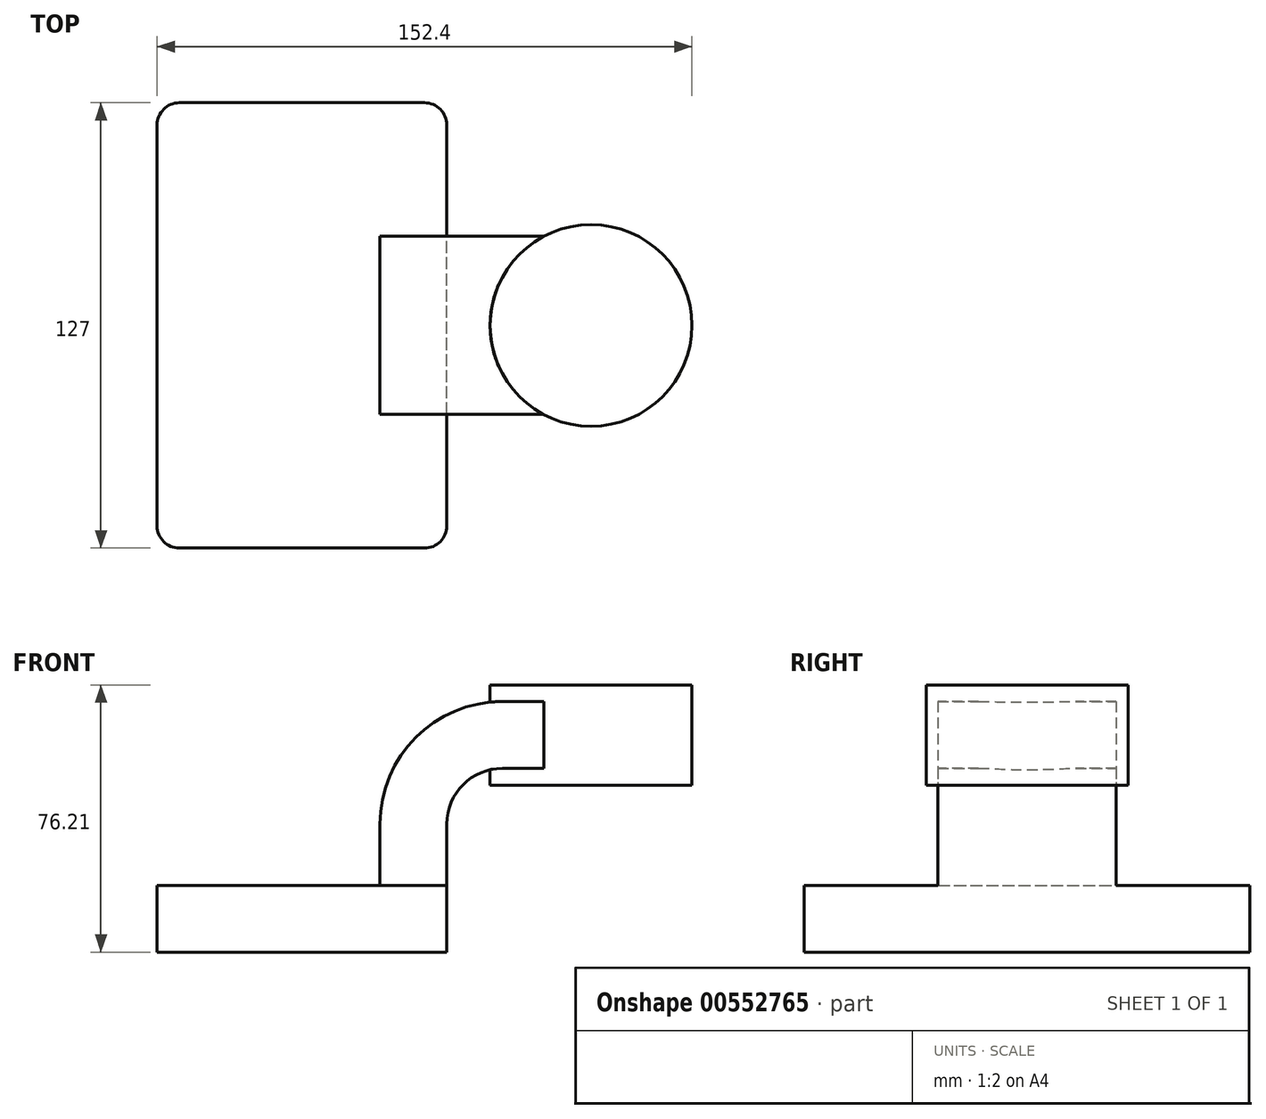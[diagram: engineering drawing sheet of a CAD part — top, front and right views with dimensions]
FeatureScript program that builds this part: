
annotation { "Feature Type Name" : "Feature", "Feature Type Description" : "" }
export const myFeature = defineFeature(function(context is Context, id is Id, definition is map)
    precondition{}
    {
        {
            var Q0;
            Q0=qCreatedBy(makeId("Front.planeOp"),FACE);
            var sketch = newSketch(context, id + "F0", { "sketchPlane" : qUnion([Q0])});
            skLineSegment(sketch, "E0.bottom", {"start": v(-41.28, 9.52) * mm, "end": v(41.28, 9.52) * mm});
            skLineSegment(sketch, "E0.top", {"start": v(-41.28, -9.53) * mm, "end": v(41.28, -9.53) * mm});
            skLineSegment(sketch, "E0.left", {"start": v(-41.28, 9.52) * mm, "end": v(-41.28, -9.53) * mm});
            skLineSegment(sketch, "E0.right", {"start": v(41.28, 9.52) * mm, "end": v(41.28, -9.53) * mm});
            skPoint(sketch, "E0.middle", {"position": v(0, 0) * mm});
            skLineSegment(sketch, "E1.bottom", {"start": v(111.13, 38.1) * mm, "end": v(60.33, 38.1) * mm});
            skLineSegment(sketch, "E1.top", {"start": v(111.13, 66.68) * mm, "end": v(60.33, 66.68) * mm});
            skLineSegment(sketch, "E1.left", {"start": v(111.13, 38.1) * mm, "end": v(111.13, 66.68) * mm});
            skLineSegment(sketch, "E1.right", {"start": v(60.33, 38.1) * mm, "end": v(60.33, 66.67) * mm});
            skPoint(sketch, "E1.middle", {"position": v(85.73, 52.39) * mm});
            skLineSegment(sketch, "E2", {"start": v(41.28, 9.52) * mm, "end": v(41.28, 27) * mm});
            skArc(sketch, "E3", {"start": v(41.28, 27) * mm, "mid": v(45.92, 38.23) * mm, "end": v(57.15, 42.88) * mm});
            skLineSegment(sketch, "E4", {"start": v(57.15, 42.88) * mm, "end": v(82.37, 42.88) * mm});
            skLineSegment(sketch, "E5.0", {"start": v(57.15, 61.93) * mm, "end": v(82.37, 61.93) * mm});
            skArc(sketch, "E5.1", {"start": v(22.23, 27) * mm, "mid": v(32.45, 51.7) * mm, "end": v(57.15, 61.93) * mm});
            skLineSegment(sketch, "E5.2", {"start": v(22.23, 9.53) * mm, "end": v(22.22, 27) * mm});
            skLineSegment(sketch, "E6", {"start": v(82.37, 38.1) * mm, "end": v(82.37, 66.68) * mm});
            skPoint(sketch, "E6.startSnap0", {"position": v(85.73, 38.1) * mm});
            skFitSpline(sketch, "E7", {"points": [v(-41.28, 9.53) * mm, v(57.15, 61.93) * mm], "startDerivative": vector(74.57, 123.73) * mm, "endDerivative": vector(128.97, -1.08) * mm});
            skSolve(sketch);
        }
        {
            var Q0;
            Q0=makeQuery(id+"F0.imprint","IMPRINT",FACE,{"disambiguationData":[TD([[makeQuery(id+"F0.imprint","IMPRINT",EDGE,{"derivedFrom":sQuery(id+"F0.wireOp",EDGE,"E0.top")}),1.0]])]});
            extrude(context, id + "F1", {"entities" : qUnion([Q0]), "endBound" : BoundingType.SYMMETRIC, "depth" : 127 * mm, "offsetDistance" : 25.4 * mm});
        }
        {
            var Q0;
            {var subQ1=sQuery(id+"F0.wireOp",EDGE,"E2");Q0=makeQuery(id+"F0.imprint","IMPRINT",FACE,{"disambiguationData":[TD([[makeQuery(id+"F0.imprint","IMPRINT",EDGE,{"derivedFrom":subQ1}),1.0]])]});}
            var Q1;
            {var subQ0=sQuery(id+"F0.wireOp",EDGE,"E4");var subQ1=sQuery(id+"F0.wireOp",EDGE,"E1.right");var subQ2=makeQuery(id+"F0.imprint","INTERSECT",VERTEX,{"derivedFrom":[subQ1,subQ0]});Q1=makeQuery(id+"F0.imprint","IMPRINT",FACE,{"disambiguationData":[TD([[makeQuery(id+"F0.imprint","IMPRINT",EDGE,{"disambiguationData":[TD([[subQ2,-1.0]])],"derivedFrom":subQ1}),-1.0]])]});}
            extrude(context, id + "F2", {"entities" : qUnion([Q0, Q1]), "operationType" : NewBodyOperationType.ADD, "endBound" : BoundingType.SYMMETRIC, "depth" : 50.8 * mm, "offsetDistance" : 25.4 * mm});
        }
        {
            var Q0;
            Q0=makeQuery(id+"F0.imprint","IMPRINT",FACE,{"disambiguationData":[TD([[makeQuery(id+"F0.imprint","IMPRINT",EDGE,{"derivedFrom":sQuery(id+"F0.wireOp",EDGE,"E5.1")}),1.0]])]});
            extrude(context, id + "F3", {"entities" : qUnion([Q0]), "operationType" : NewBodyOperationType.ADD, "endBound" : BoundingType.SYMMETRIC, "depth" : 15.88 * mm, "offsetDistance" : 25.4 * mm});
        }
        {
            var Q0;
            {var subQ4=sQuery(id+"F0.wireOp",EDGE,"E1.left");Q0=makeQuery(id+"F0.imprint","IMPRINT",FACE,{"disambiguationData":[TD([[makeQuery(id+"F0.imprint","IMPRINT",EDGE,{"derivedFrom":subQ4}),1.0]])]});}
            var Q1;
            Q1=sQuery(id+"F0.wireOp",EDGE,"E6");
            revolve(context, id + "F4", {"operationType" : NewBodyOperationType.ADD, "entities" : qUnion([Q0]), "axis" : qUnion([Q1]), "revolveType" : RevolveType.FULL});
        }
        {
            var Q0;
            Q0=makeQuery(id+"F1.opExtrude","CAP_EDGE",EDGE,{"disambiguationData":[OSD([sQuery(id+"F0.wireOp",EDGE,"E0.right")])],"isStart":true});
            var Q1;
            Q1=makeQuery(id+"F1.opExtrude","CAP_EDGE",EDGE,{"disambiguationData":[OSD([sQuery(id+"F0.wireOp",EDGE,"E0.left")])],"isStart":true});
            var Q2;
            Q2=makeQuery(id+"F1.opExtrude","CAP_EDGE",EDGE,{"disambiguationData":[OSD([sQuery(id+"F0.wireOp",EDGE,"E0.left")])],"isStart":false});
            var Q3;
            Q3=makeQuery(id+"F1.opExtrude","CAP_EDGE",EDGE,{"disambiguationData":[OSD([sQuery(id+"F0.wireOp",EDGE,"E0.right")])],"isStart":false});
            fillet(context, id + "F5", {"entities" : qUnion([Q0, Q1, Q2, Q3]), "radius" : 6.35 * mm, "tangentPropagation" : true, "allowEdgeOverflow" : false});
        }
    });
